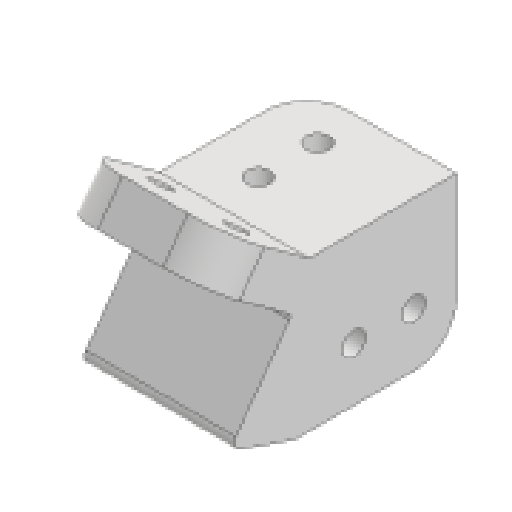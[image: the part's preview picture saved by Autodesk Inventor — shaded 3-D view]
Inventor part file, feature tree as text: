
AUTODESK INVENTOR PART (.ipt)
format: ipt  version: 2025 (Build 290162000, 162)  size: 186,368 bytes
history: native  units: mm
features: reference x8, extrude x4, sketch x4, projected_geometry x4, other x4, fillet x3
ambient origin geometry x8: Origin, YZ Plane, XZ Plane, XY Plane, X Axis, Y Axis, Z Axis, Center Point
bodies: Solid1 (feature_tree)
feature tree (27):
  extrude  "Extrusion1"  Depth=38.1mm
  extrude  "Extrusion2"  Depth=10.0mm TaperAngle=0.0deg
  extrude  "Extrusion3"  Depth=35.4mm TaperAngle=0.0deg
  extrude  "Extrusion4"  Depth=35.4mm TaperAngle=0.0deg
  fillet  "Fillet1"  Radius=2.6mm
  fillet  "Fillet2"  Radius=35.4mm
  fillet  "Fillet3"  Radius=10.0mm
  sketch  "Sketch1"  dims[d0=25.4mm d1=38.1mm]
  sketch  "Sketch2"  dims[d2=5.5mm d3=10.0mm d4=0.0mm]
  reference  "Reference1"
  reference  "Reference2"
  reference  "Reference3"
  reference  "Reference4"
  reference  "Reference5"
  reference  "Reference6"
  reference  "Reference7"
  reference  "Reference8"
  projected_geometry  "Projected Loop1"
  sketch  "Sketch3"  dims[d5=10.0mm d8=35.4mm d9=0.0mm]
  projected_geometry  "Projected Loop2"
  projected_geometry  "Projected Loop3"
  sketch  "Sketch4"  dims[d10=10.0mm d11=35.4mm d12=0.0mm d13=2.6mm d14=35.4mm d15=0.0mm d16=10.0mm d17=2.0mm d18=1.0mm d7=0.5mm]
  projected_geometry  "Projected Loop4"
  other  "<userpath>\Desktop\puppycat\woodhouseMK1.iam"
  other  "woodhouseMK1.iam"
  other  "12inStrut:1"
  other  "trackBase:1"
